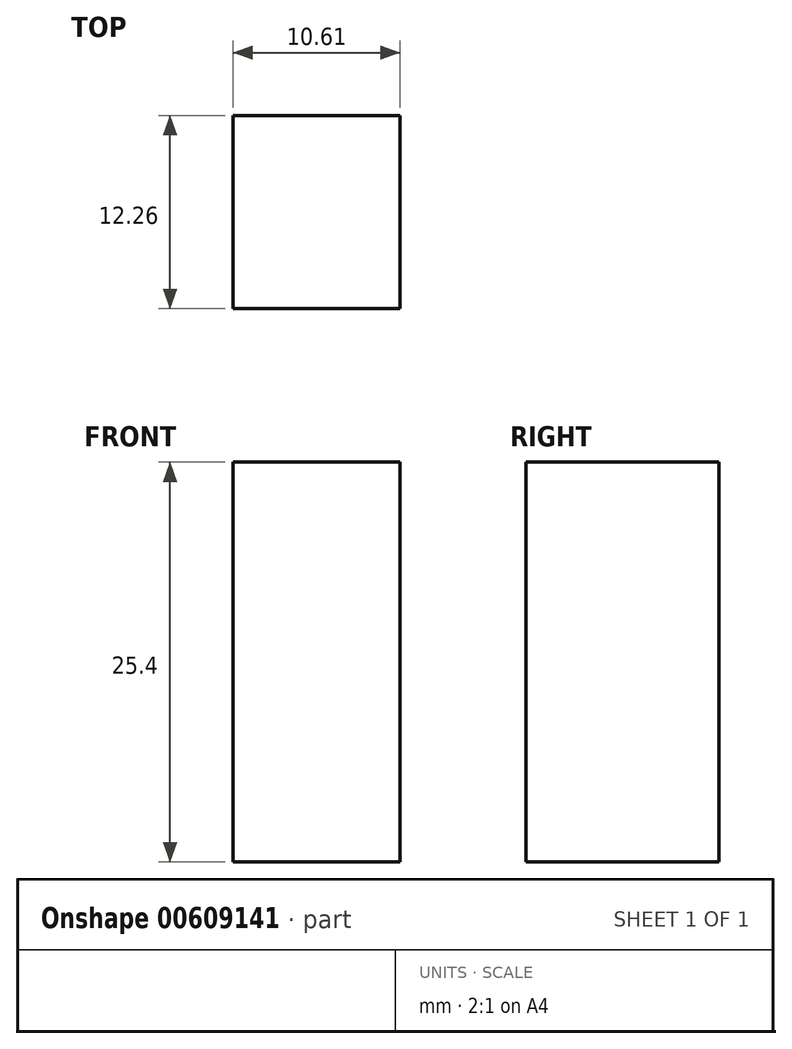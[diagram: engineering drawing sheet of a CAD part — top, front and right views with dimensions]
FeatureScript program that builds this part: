
annotation { "Feature Type Name" : "Feature", "Feature Type Description" : "" }
export const myFeature = defineFeature(function(context is Context, id is Id, definition is map)
    precondition{}
    {
        {
            var Q0;
            Q0=qCreatedBy(makeId("Top.planeOp"),FACE);
            var sketch = newSketch(context, id + "F0", { "sketchPlane" : qUnion([Q0])});
            skLineSegment(sketch, "E0.bottom", {"start": v(34.5, -22.9) * mm, "end": v(23.88, -22.9) * mm});
            skLineSegment(sketch, "E0.top", {"start": v(34.5, -10.64) * mm, "end": v(23.88, -10.64) * mm});
            skLineSegment(sketch, "E0.left", {"start": v(34.5, -22.9) * mm, "end": v(34.5, -10.64) * mm});
            skLineSegment(sketch, "E0.right", {"start": v(23.88, -22.9) * mm, "end": v(23.88, -10.64) * mm});
            skSolve(sketch);
        }
        {
            var Q0;
            Q0=makeQuery(id+"F0.imprint","IMPRINT",FACE,{"disambiguationData":[TD([[makeQuery(id+"F0.imprint","IMPRINT",EDGE,{"derivedFrom":sQuery(id+"F0.wireOp",EDGE,"E0.bottom")}),-1.0]])]});
            var Q1;
            Q1 = qSketchRegion(id + "F0", true);
            extrude(context, id + "F1", {"entities" : qUnion([Q0, Q1]), "depth" : 25.4 * mm, "offsetDistance" : 25.4 * mm});
        }
    });
